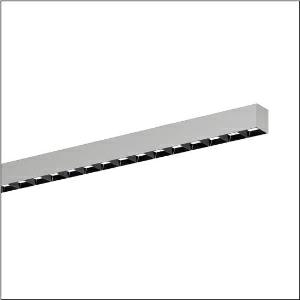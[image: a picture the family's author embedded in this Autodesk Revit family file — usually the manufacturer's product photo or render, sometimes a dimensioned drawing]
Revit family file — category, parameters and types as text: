
# Revit family: silica_r__21_51mx24dc4asb_83d0
name_source: partatom
category: Lighting Fixtures
units: mm (PartAtom-declared; Revit-internal decimal feet)

## family parameters
Cut with Voids When Loaded = No
Host = Face
Light Source = No
Part Type = Normal
Room Calculation Point = No
Round Connector Dimension = Use Diameter
Shared = No

## types (1)
- --- (1 x LED, 10800 lm, 73.7 W, 4000K)
    Apparent Load = 74 VA
    CIE Flux Codes = 74 94 99 100 100
    Color Rendering = 80
    Color Temperature = 4000K
    Default Elevation = 1800 mm
    Description = Silica® 21, office luminaire, primary light control with darklight reflector, of PMMA, black, CAT 2 (L<= 3000cd/m²), light emission: direct distribution, primary light characteristic: asymmetric, installation type: surface-mounted, LED, rated luminous flux: 10.800lm, luminous efficacy: 147lm/W, light colour: 840, colour temperature: 4000K, with terminal, 3+2-pole, max. 2.5mm², mains connection: 220..240V, AC, 50/60Hz, rated input power: 73.7W, luminaire housing, of aluminium, metallic grey (RAL 9006), length: 3.004mm, width: 53mm, height: 53mm, protection rating (complete): IP20, insulation class (complete): insulation class I (protective earthing), certification: CE, permissible operating ambient temperature: 0..+35°C, standard: EN 50419, packaging unit: 1 piece
    Height = 0 mm  [stored 0 ft]
    Lamp = 1 x LED
    Lamp Light Flux = 10800 lm
    Lamp Power = 73.7 W
    Lamp count = 1
    Length = 3004 mm
    Luminous efficacy = 147 lm/W
    Manufacturer = Siteco
    ModVariant = No
    Model = 51MX24DC4ASB
    Mounting Place = Ceiling
    Mounting Type = Recessed
    Number of Poles = 1
    OnlyDefault = Yes
    Power Factor = 1
    Product Name = Silica® 21
    Product group = office luminaire | ceiling recessed
    ProductGroupID = 400
    Protection Class = Protection class I
    Protection Degree = IP 20
    RLX_Detail_Level = 1
    RLX_Emergency_Light_Flux = 0 lm
    RLX_Emergency_Type = 0
    RLX_Emergency_Type_DB = No
    RlxData = <blob elided: 65221 chars, md5=dd2dfadf>
    Socket = socket
    Standby Power = 0 W
    System Light Flux = 10800 lm
    System Power = 74 W
    Type Comments = factory setting: luminous flux: 100 % | dim-lin: 254 | 418 mA
    Type Image = l_1335929.jpg
    URL = http://relux.com
    VarID = @adj_092117
    Voltage = 0 V
    Weight = 0.00 kg
    Width = 53 mm

note: [stored X ft] marks values corroborated as IEEE doubles in the binary element streams (Revit-internal decimal feet)

## geometry (parser evidence)
native form markers: Blend x4, Sweep x11
no freeform markers — native parametric forms only
